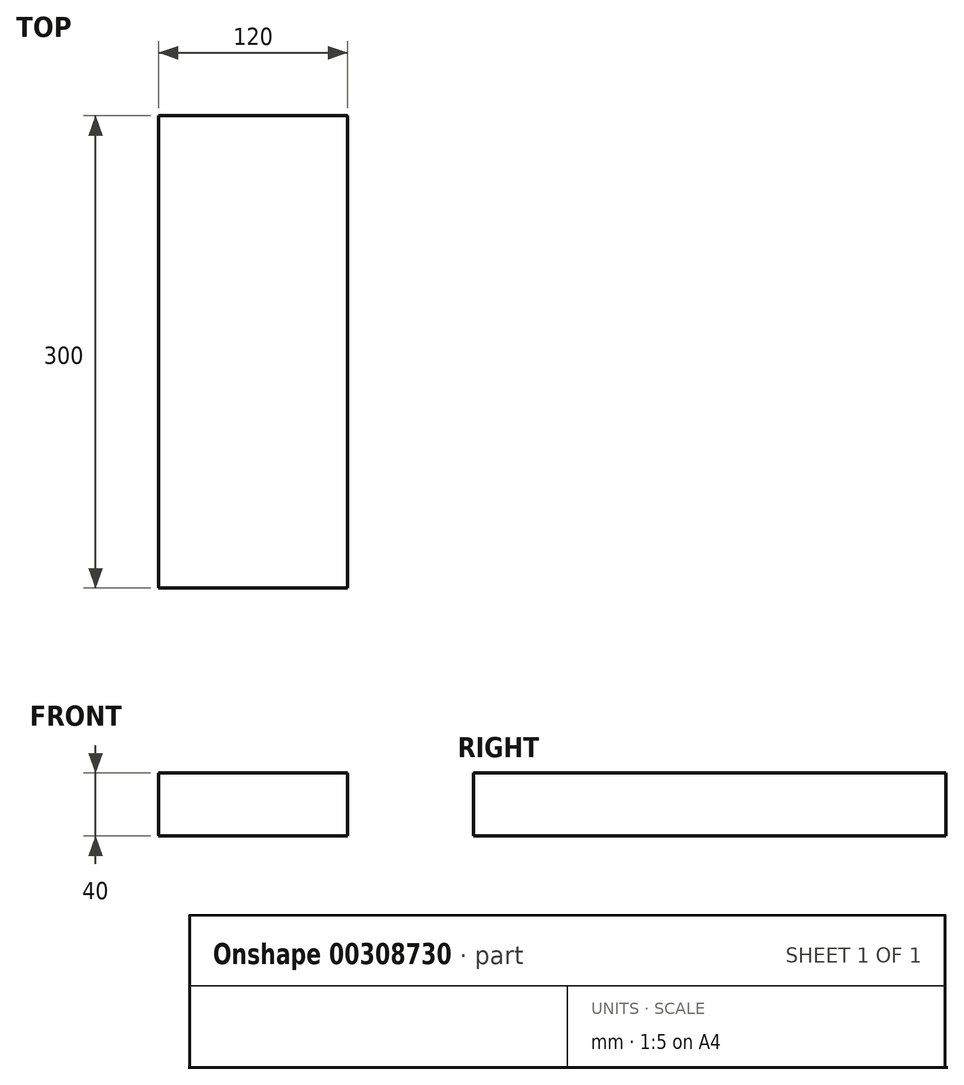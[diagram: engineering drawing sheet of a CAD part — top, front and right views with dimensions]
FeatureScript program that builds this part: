
annotation { "Feature Type Name" : "Feature", "Feature Type Description" : "" }
export const myFeature = defineFeature(function(context is Context, id is Id, definition is map)
    precondition{}
    {
        {
            var Q0;
            Q0=qCreatedBy(makeId("Top.planeOp"),FACE);
            var sketch = newSketch(context, id + "F0", { "sketchPlane" : qUnion([Q0])});
            skLineSegment(sketch, "E0.bottom", {"start": v(60, -150) * mm, "end": v(-60, -150) * mm});
            skLineSegment(sketch, "E0.top", {"start": v(60, 150) * mm, "end": v(-60, 150) * mm});
            skLineSegment(sketch, "E0.left", {"start": v(60, -150) * mm, "end": v(60, 150) * mm});
            skLineSegment(sketch, "E0.right", {"start": v(-60, -150) * mm, "end": v(-60, 150) * mm});
            skPoint(sketch, "E0.middle", {"position": v(0, 0) * mm});
            skSolve(sketch);
        }
        {
            var Q0;
            Q0=makeQuery(id+"F0.imprint","IMPRINT",FACE,{"disambiguationData":[TD([[makeQuery(id+"F0.imprint","IMPRINT",EDGE,{"derivedFrom":sQuery(id+"F0.wireOp",EDGE,"E0.bottom")}),-1.0]])]});
            extrude(context, id + "F1", {"entities" : qUnion([Q0]), "oppositeDirection" : true, "depth" : 40 * mm});
        }
    });
